# Revit family: SN1008 updated
name_source: partatom
category: Lighting Fixtures
units: mm (PartAtom-declared; Revit-internal decimal feet)

## family parameters
Cut with Voids When Loaded = No
Host = Face
Light Source = No
Part Type = Normal
Room Calculation Point = No
Round Connector Dimension = Use Diameter
Shared = Yes

## types (4) — shared parameters
Current Amps = 50 A
Default Elevation = 48 "
Description = Flexible, Linear LED Lighting
Environment = Indoor
Frequency = 60 Hz
Has Battery Backup = No
Has Dimming = Yes
Housing Protection Rating = Consult Manufacturer Website for more Information
Increment = 1.9685 "
Initial Intensity Comments = Refer LED Strip type for Lumen Value
Input Voltage = 24VDC
LED Tape Documentation link = https://bllighting.com
LED Tape Page URL = https://bllighting.com
LED finish = LED
LED strip = Strip
Lamp Life = 50,000 Hours
Lens Material = Polycarbonate Optic
Load Classification = Lighting
Manufacturer = BL Lighting
Mounting Method = Surface Mount
Number of Poles = 1
Operating Temperature = Consult Manufacturer Website for more Information
Phase = 1
Power Factor = 1
Power Source Type = Driver
Product Documentation Link = https://bllighting.com
Product Page URL = https://bllighting.com
Profile Material = Alumnium Base Track
URL = https://bllighting.com
Version = 2020-v2.9
Voltage = 24 V
W = 0.31 "
W1 = 0.5 "
Warranty URL = https://bllighting.com

## per-type parameters (varying)
| type | Apparent Load | CCT | Color Option Available | DFN1 | DFN2 | Initial Color Comments | Lamp | Lumen Output | Max Input Current | Model | N1 | N2 | Number of LED's | Product Name | Wattage Comments |
| 180 lm per FT 1.85 W per FT - N2 | 120 VA | 2700K,3000K,3500K,4000K | 2700K,3000K,3500K,4000K | No | No | Perfomance based on 3000K Photometric Web File | LED,SMD 3528 | 180 lm/FT | 5 A | N2 | No | Yes | 18 Diodes/FT | N2 | 1.85W/FT |
| 91 lm per FT 1.00 W per FT - N1 | 34 VA | 2700K,3000K,4000K,6500K | 2700K,3000K,4000K,6500K | No | No | Perfomance based on 2700K Photometric Web File | LED,SMD2216 | 91 lm/FT | 1.40 A | N1 | Yes | No | 42 Diodes/FT | N1 | 1.0W/FT |
| 201 lm per FT 2.4 W per FT - DFN2 | 96 VA | 2400K,2700K,3000K,3500K,4000K | 2400K,2700K,3000K,3500K,4000K | No | Yes | Perfomance based on 3000K Photometric Web File |  | 201 lm/FT | 4 A | DFN2 | No | No | 146 Diodes/FT | DFN2 | 2.4W/FT |
| 84 lm per FT 1.00 W per FT - DFN1 | 96 VA | 2400K,2700K,3000K,3500K,4000K | 2400K,2700K,3000K,3500K,4000K | Yes | No | Perfomance based on 3000K Photometric Web File |  | 84 lm/FT | 4 A | DFN1 | No | No | 146 Diodes/FT | DFN1 | 1.0W/FT |

## geometry (parser evidence)
native form markers: Sweep x35
no freeform markers — native parametric forms only
